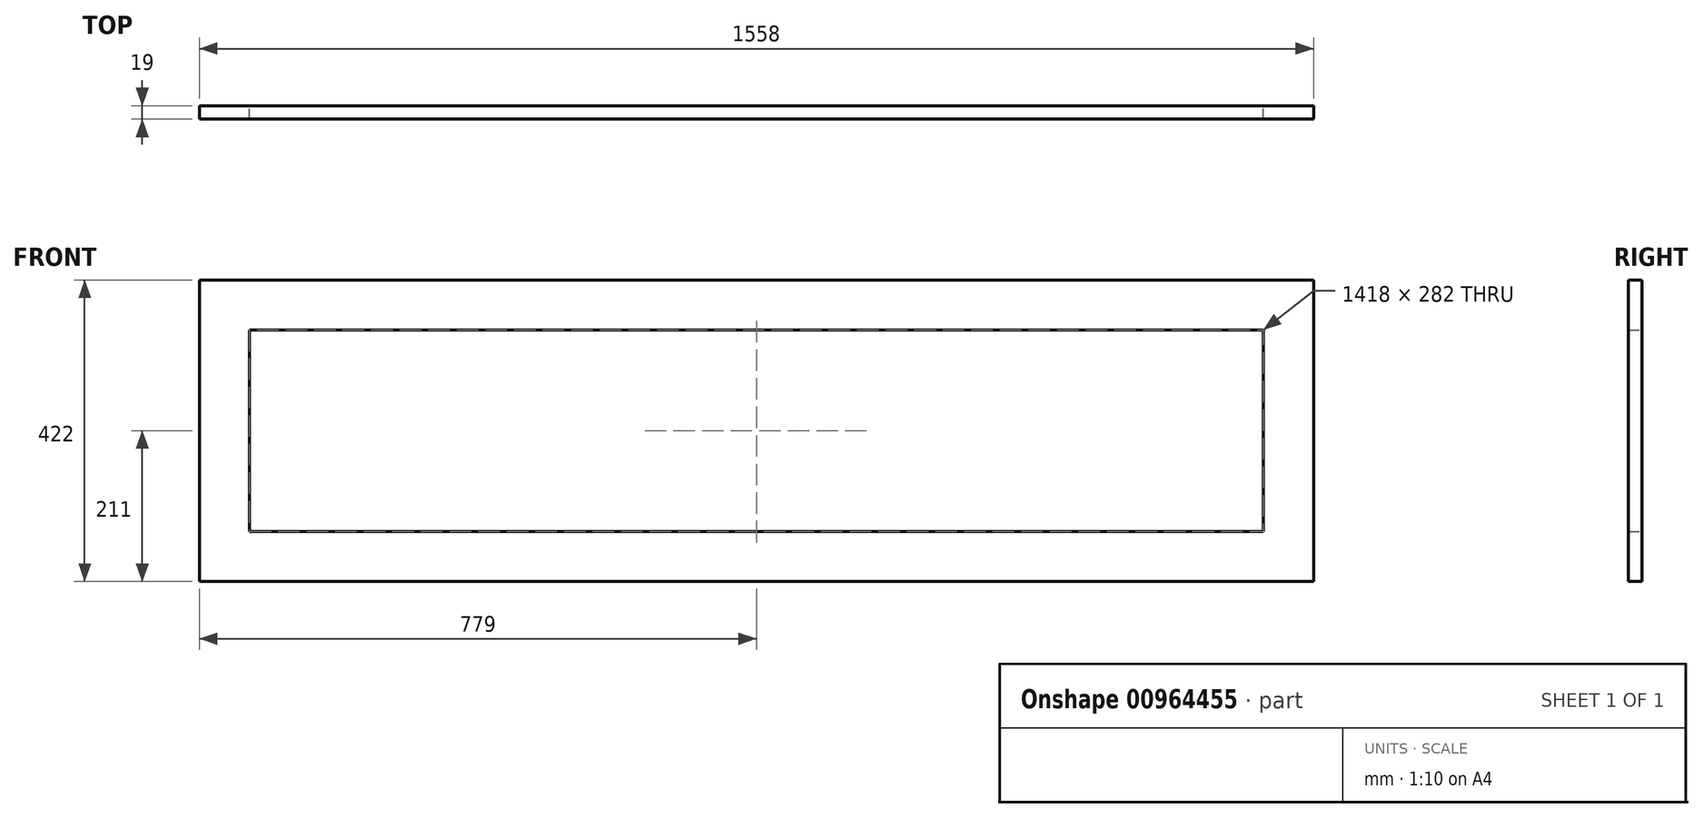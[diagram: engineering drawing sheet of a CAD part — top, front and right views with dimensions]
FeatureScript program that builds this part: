
annotation { "Feature Type Name" : "Feature", "Feature Type Description" : "" }
export const myFeature = defineFeature(function(context is Context, id is Id, definition is map)
    precondition{}
    {
        {
            var Q0;
            Q0=qCreatedBy(makeId("Front.planeOp"),FACE);
            var sketch = newSketch(context, id + "F0", { "sketchPlane" : qUnion([Q0])});
            skLineSegment(sketch, "E0.bottom", {"start": v(0, 0) * mm, "end": v(1558, 0) * mm});
            skLineSegment(sketch, "E0.top", {"start": v(0, 422) * mm, "end": v(1558, 422) * mm});
            skLineSegment(sketch, "E0.left", {"start": v(0, 0) * mm, "end": v(0, 422) * mm});
            skLineSegment(sketch, "E0.right", {"start": v(1558, 0) * mm, "end": v(1558, 422) * mm});
            skLineSegment(sketch, "E1.0", {"start": v(70, 352) * mm, "end": v(1488, 352) * mm});
            skLineSegment(sketch, "E1.1", {"start": v(70, 70) * mm, "end": v(70, 352) * mm});
            skLineSegment(sketch, "E1.2", {"start": v(70, 70) * mm, "end": v(1488, 70) * mm});
            skLineSegment(sketch, "E1.3", {"start": v(1488, 70) * mm, "end": v(1488, 352) * mm});
            skSolve(sketch);
        }
        {
            var Q0;
            Q0 = qSketchRegion(id + "F0", true);
            extrude(context, id + "F1", {"entities" : qUnion([Q0]), "depth" : 19 * mm, "offsetDistance" : 25 * mm});
        }
    });
